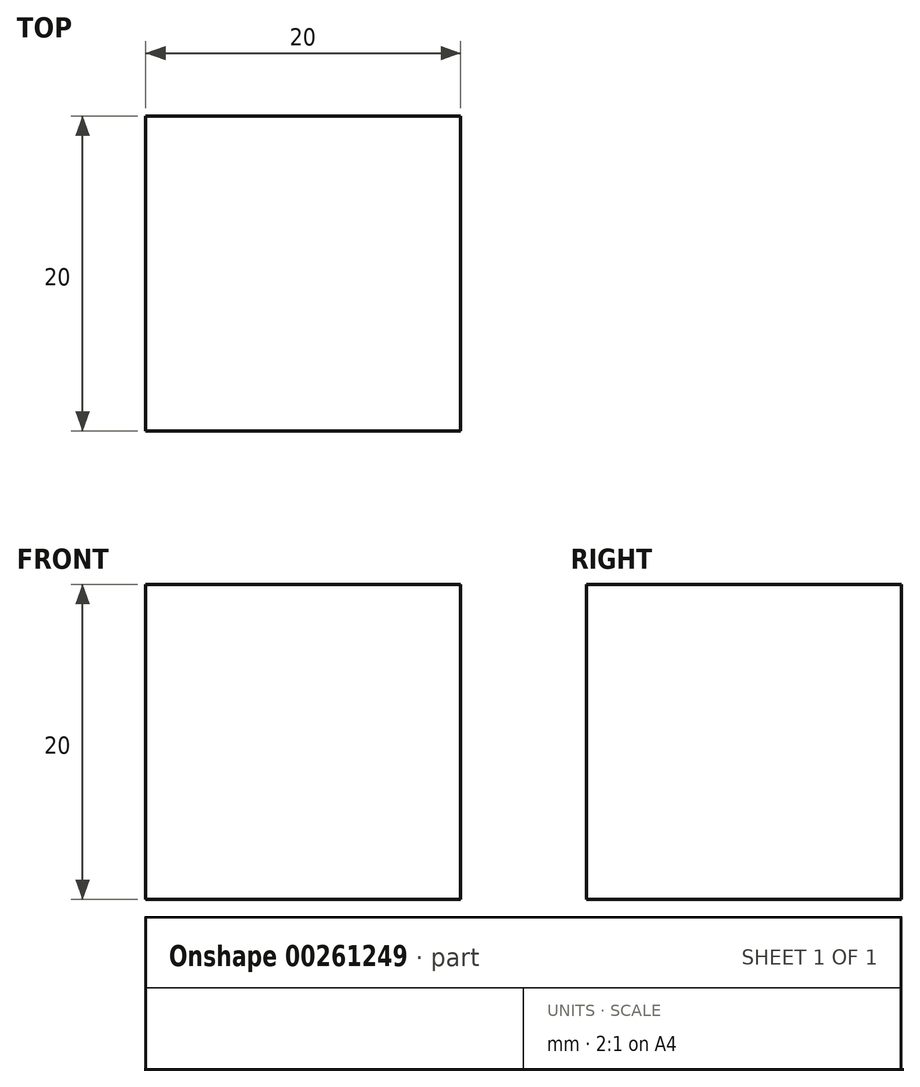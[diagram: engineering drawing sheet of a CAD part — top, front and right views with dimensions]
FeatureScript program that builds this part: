
annotation { "Feature Type Name" : "Feature", "Feature Type Description" : "" }
export const myFeature = defineFeature(function(context is Context, id is Id, definition is map)
    precondition{}
    {
        {
            var Q0;
            Q0=qCreatedBy(makeId("Front.planeOp"),FACE);
            var sketch = newSketch(context, id + "F0", { "sketchPlane" : qUnion([Q0])});
            skLineSegment(sketch, "E0.bottom", {"start": v(-17.06, 0) * mm, "end": v(-37.06, 0) * mm});
            skLineSegment(sketch, "E0.top", {"start": v(-17.06, 20) * mm, "end": v(-37.06, 20) * mm});
            skLineSegment(sketch, "E0.left", {"start": v(-17.06, 0) * mm, "end": v(-17.06, 20) * mm});
            skLineSegment(sketch, "E0.right", {"start": v(-37.06, 0) * mm, "end": v(-37.06, 20) * mm});
            skSolve(sketch);
        }
        {
            var Q0;
            Q0 = qSketchRegion(id + "F0", true);
            extrude(context, id + "F1", {"entities" : qUnion([Q0]), "depth" : 20 * mm});
        }
    });
